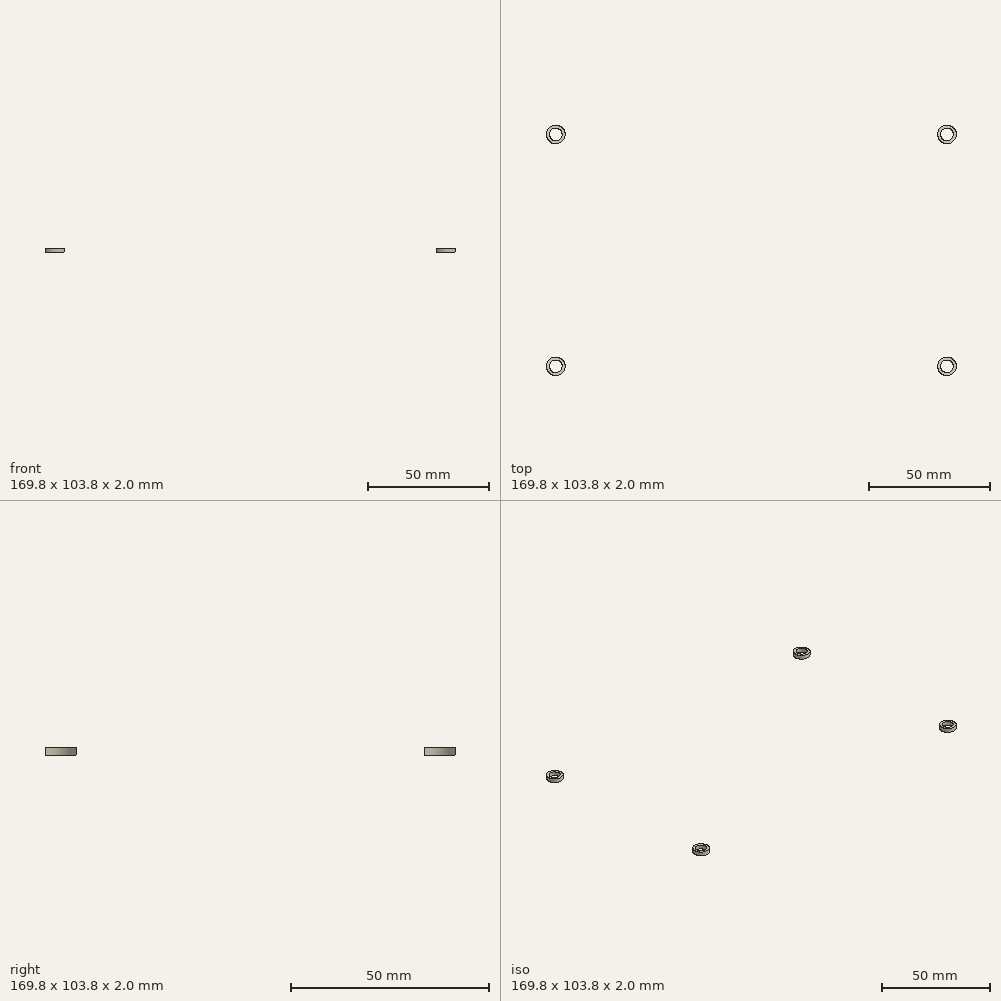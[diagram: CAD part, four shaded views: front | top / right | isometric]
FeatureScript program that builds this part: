
annotation { "Feature Type Name" : "Feature", "Feature Type Description" : "" }
export const myFeature = defineFeature(function(context is Context, id is Id, definition is map)
    precondition{}
    {
        {
            var Q0;
            Q0=qCreatedBy(makeId("Top.planeOp"),FACE);
            var sketch = newSketch(context, id + "F0", { "sketchPlane" : qUnion([Q0])});
            skLineSegment(sketch, "E0.bottom", {"start": v(81, -48) * mm, "end": v(-81, -48) * mm, "construction": true});
            skLineSegment(sketch, "E0.top", {"start": v(81, 48) * mm, "end": v(-81, 48) * mm, "construction": true});
            skLineSegment(sketch, "E0.left", {"start": v(81, -48) * mm, "end": v(81, 48) * mm, "construction": true});
            skLineSegment(sketch, "E0.right", {"start": v(-81, -48) * mm, "end": v(-81, 48) * mm, "construction": true});
            skPoint(sketch, "E0.middle", {"position": v(0, 0) * mm});
            skPoint(sketch, "E1", {"position": v(-81, 48) * mm});
            skPoint(sketch, "E2", {"position": v(81, 48) * mm});
            skPoint(sketch, "E3", {"position": v(81, -48) * mm});
            skPoint(sketch, "E4", {"position": v(-81, -48) * mm});
            skCircle(sketch, "E5", {"center": v(-81, 48) * mm, "radius": 3.88 * mm});
            skCircle(sketch, "E6", {"center": v(-81, -48) * mm, "radius": 3.88 * mm});
            skCircle(sketch, "E7", {"center": v(81, 48) * mm, "radius": 3.88 * mm});
            skCircle(sketch, "E8", {"center": v(81, -48) * mm, "radius": 3.88 * mm});
            skCircle(sketch, "E9", {"center": v(-81, 48) * mm, "radius": 2.62 * mm});
            skCircle(sketch, "E10", {"center": v(-81, -48) * mm, "radius": 2.62 * mm});
            skCircle(sketch, "E11", {"center": v(81, -48) * mm, "radius": 2.62 * mm});
            skCircle(sketch, "E12", {"center": v(81, 48) * mm, "radius": 2.62 * mm});
            skSolve(sketch);
        }
        {
            var Q0;
            Q0=makeQuery(id+"F0.imprint","IMPRINT",FACE,{"disambiguationData":[TD([[makeQuery(id+"F0.imprint","IMPRINT",EDGE,{"derivedFrom":sQuery(id+"F0.wireOp",EDGE,"E5")}),1.0]])]});
            var Q1;
            Q1=makeQuery(id+"F0.imprint","IMPRINT",FACE,{"disambiguationData":[TD([[makeQuery(id+"F0.imprint","IMPRINT",EDGE,{"derivedFrom":sQuery(id+"F0.wireOp",EDGE,"E6")}),1.0]])]});
            var Q2;
            Q2=makeQuery(id+"F0.imprint","IMPRINT",FACE,{"disambiguationData":[TD([[makeQuery(id+"F0.imprint","IMPRINT",EDGE,{"derivedFrom":sQuery(id+"F0.wireOp",EDGE,"E7")}),1.0]])]});
            var Q3;
            Q3=makeQuery(id+"F0.imprint","IMPRINT",FACE,{"disambiguationData":[TD([[makeQuery(id+"F0.imprint","IMPRINT",EDGE,{"derivedFrom":sQuery(id+"F0.wireOp",EDGE,"E8")}),1.0]])]});
            extrude(context, id + "F1", {"entities" : qUnion([Q0, Q1, Q2, Q3]), "depth" : 2 * mm, "offsetDistance" : 25 * mm});
        }
    });
